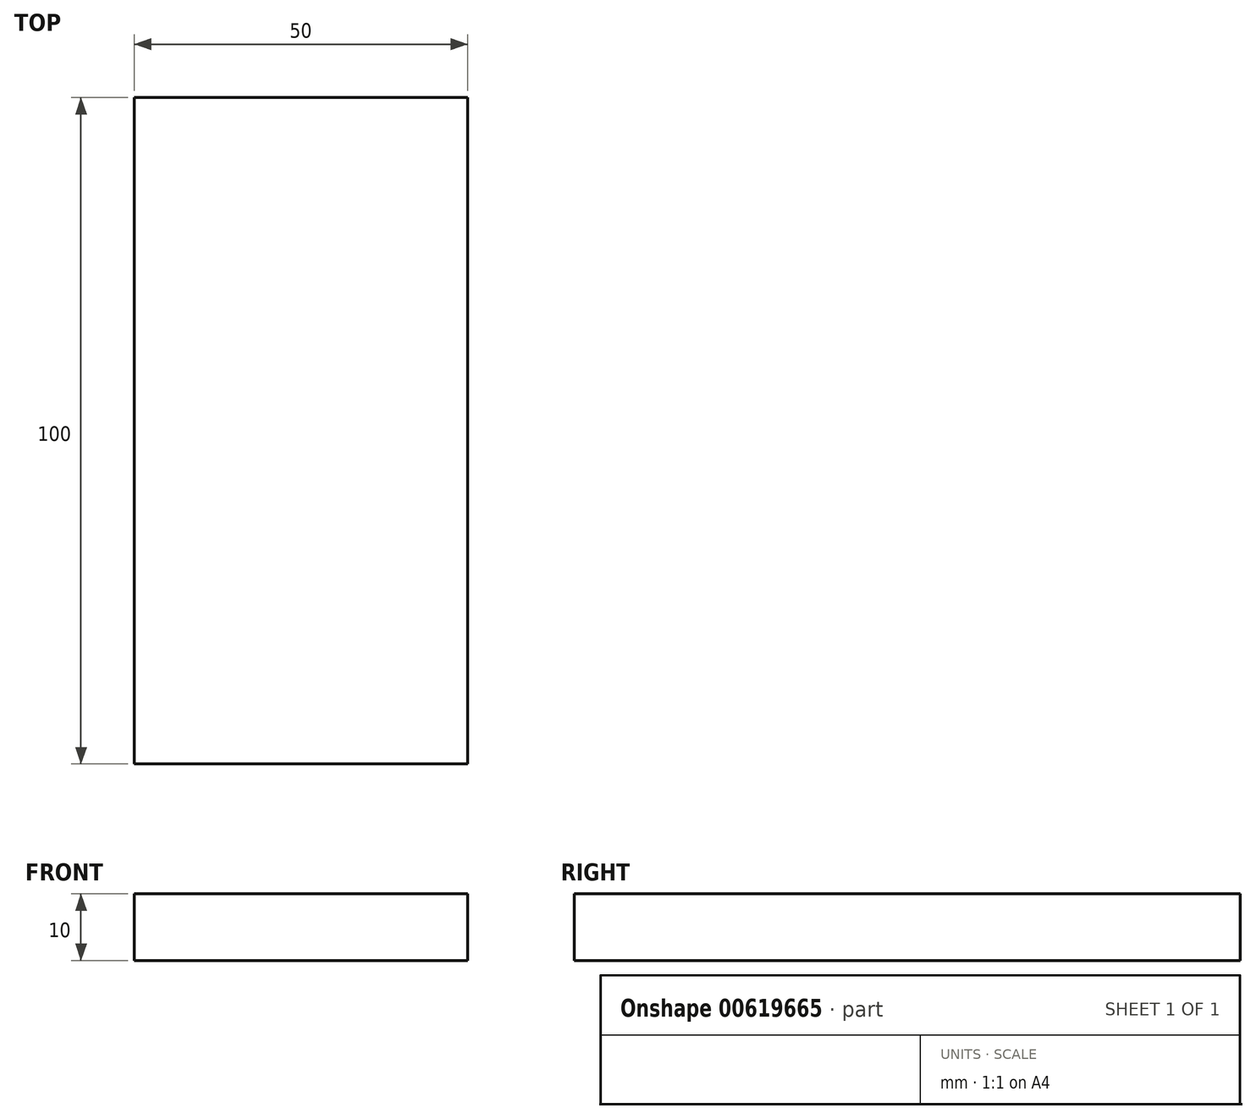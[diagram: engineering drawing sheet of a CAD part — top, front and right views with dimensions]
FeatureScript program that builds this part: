
annotation { "Feature Type Name" : "Feature", "Feature Type Description" : "" }
export const myFeature = defineFeature(function(context is Context, id is Id, definition is map)
    precondition{}
    {
        {
            var Q0;
            Q0=qCreatedBy(makeId("Top.planeOp"),FACE);
            var sketch = newSketch(context, id + "F0", { "sketchPlane" : qUnion([Q0])});
            skLineSegment(sketch, "E0.bottom", {"start": v(-21.54, 60.22) * mm, "end": v(28.46, 60.22) * mm});
            skLineSegment(sketch, "E0.top", {"start": v(-21.54, -39.78) * mm, "end": v(28.46, -39.78) * mm});
            skLineSegment(sketch, "E0.left", {"start": v(-21.54, 60.22) * mm, "end": v(-21.54, -39.78) * mm});
            skLineSegment(sketch, "E0.right", {"start": v(28.46, 60.22) * mm, "end": v(28.46, -39.78) * mm});
            skSolve(sketch);
        }
        {
            var Q0;
            Q0=makeQuery(id+"F0.imprint","IMPRINT",FACE,{"disambiguationData":[TD([[makeQuery(id+"F0.imprint","IMPRINT",EDGE,{"derivedFrom":sQuery(id+"F0.wireOp",EDGE,"E0.bottom")}),-1.0]])]});
            extrude(context, id + "F1", {"entities" : qUnion([Q0]), "depth" : 10 * mm, "offsetDistance" : 25 * mm});
        }
    });
